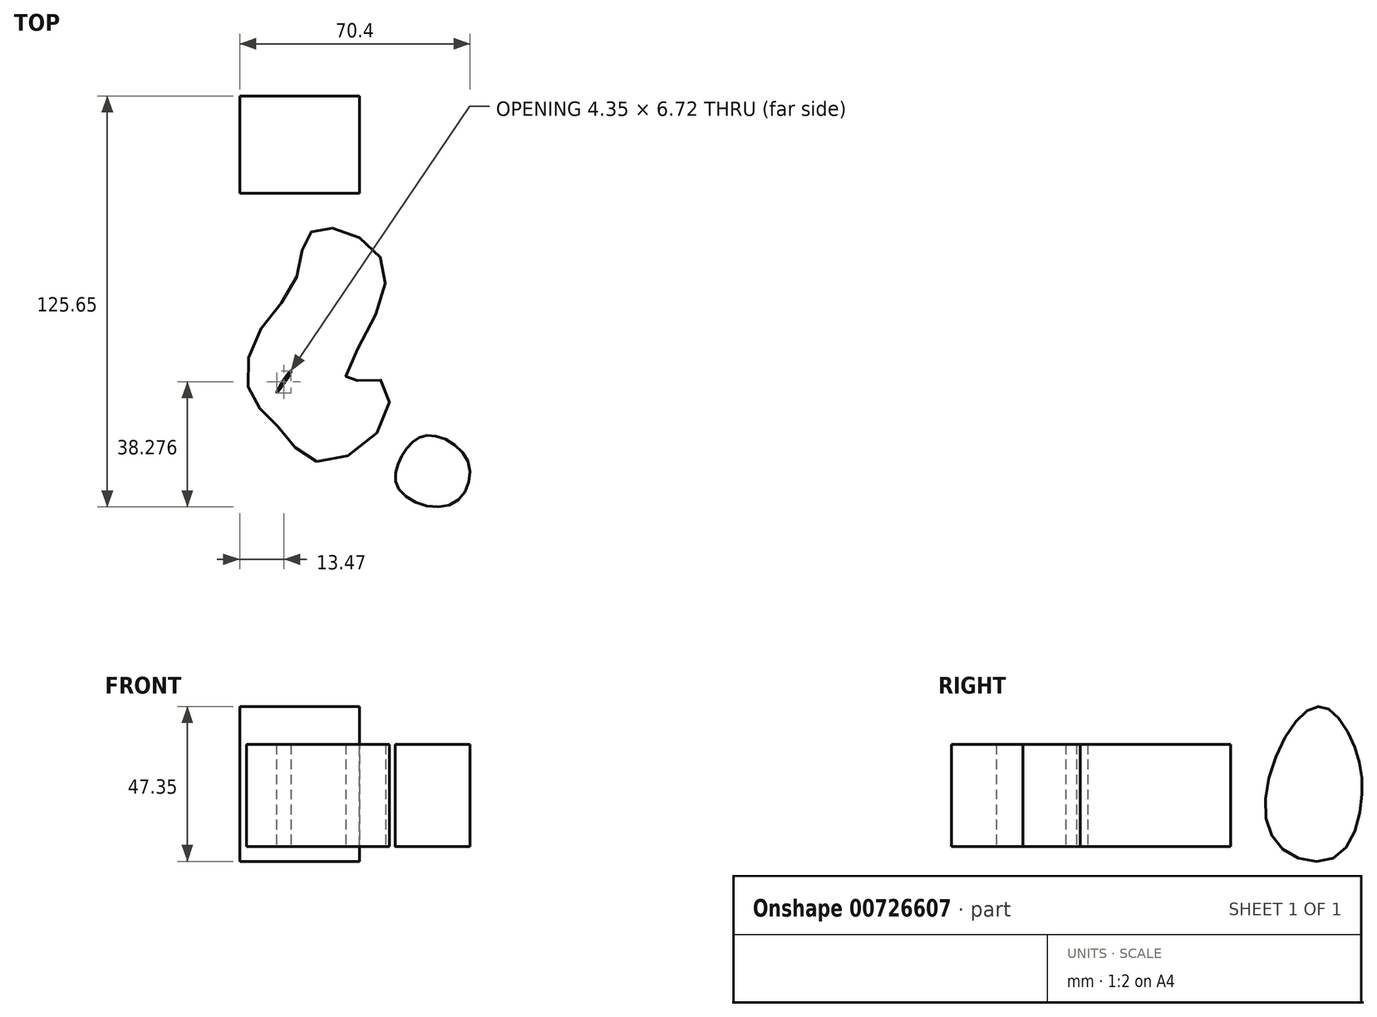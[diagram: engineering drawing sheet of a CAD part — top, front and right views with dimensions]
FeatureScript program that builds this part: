
annotation { "Feature Type Name" : "Feature", "Feature Type Description" : "" }
export const myFeature = defineFeature(function(context is Context, id is Id, definition is map)
    precondition{}
    {
        {
            var Q0;
            Q0=qCreatedBy(makeId("Top.planeOp"),FACE);
            var sketch = newSketch(context, id + "F0", { "sketchPlane" : qUnion([Q0])});
            skFitSpline(sketch, "E0", {"points": [v(23.55, -40.1) * mm, v(44.04, -28.28) * mm, v(42.47, -14.88) * mm, v(32.81, -15.47) * mm, v(39.9, 1.48) * mm, v(43.65, 21.18) * mm, v(29.86, 31.04) * mm, v(20.6, 28.87) * mm, v(17.24, 15.67) * mm, v(4.83, -2.27) * mm, v(3.45, -20) * mm, v(12.32, -30.05) * mm, v(23.55, -40.1) * mm]});
            skFitSpline(sketch, "E1", {"points": [v(48.7, -48.67) * mm, v(49.87, -37.83) * mm, v(57.76, -32.11) * mm, v(69.78, -40.1) * mm, v(64.65, -53.2) * mm, v(48.7, -48.67) * mm]});
            skFitSpline(sketch, "E2", {"points": [v(11.3, -19.1) * mm, v(15.69, -12.57) * mm, v(15.44, -12.44) * mm, v(11.3, -19.1) * mm]});
            skSolve(sketch);
        }
        {
            var Q0;
            Q0 = qSketchRegion(id + "F0", true);
            extrude(context, id + "F1", {"entities" : qUnion([Q0]), "depth" : 31.24 * mm, "offsetDistance" : 25.4 * mm});
        }
        {
            var Q0;
            Q0=qCreatedBy(makeId("Right.planeOp"),FACE);
            var sketch = newSketch(context, id + "F2", { "sketchPlane" : qUnion([Q0])});
            skFitSpline(sketch, "E3", {"points": [v(61.4, 42.03) * mm, v(69.48, 30.01) * mm, v(71.45, 14.45) * mm, v(63.56, -3.1) * mm, v(46.42, 0) * mm, v(42.87, 20.16) * mm, v(54.1, 41.05) * mm, v(61.4, 42.03) * mm]});
            skFitSpline(sketch, "E4", {"points": [v(56.27, 27.25) * mm, v(63.76, 23.9) * mm, v(62.97, 15.82) * mm, v(58.83, 8.34) * mm, v(51.54, 13.07) * mm, v(52.33, 22.33) * mm, v(56.27, 27.25) * mm]});
            skSolve(sketch);
        }
        {
            var Q0;
            Q0=makeQuery(id+"F2.imprint","IMPRINT",FACE,{"disambiguationData":[TD([[makeQuery(id+"F2.imprint","IMPRINT",EDGE,{"derivedFrom":sQuery(id+"F2.wireOp",EDGE,"E3")}),-1.0]])]});
            var Q1;
            Q1=makeQuery(id+"F2.imprint","IMPRINT",FACE,{"disambiguationData":[TD([[makeQuery(id+"F2.imprint","IMPRINT",EDGE,{"derivedFrom":sQuery(id+"F2.wireOp",EDGE,"E4")}),-1.0]])]});
            extrude(context, id + "F3", {"entities" : qUnion([Q0, Q1]), "depth" : 11.18 * mm, "offsetDistance" : 25.4 * mm});
        }
        {
            var Q0;
            Q0=makeQuery(id+"F3.opExtrude","CAP_FACE",FACE,{"disambiguationData":[OSD([sQuery(id+"F2.wireOp",EDGE,"E3")])],"isStart":true});
            var Q1;
            Q1=makeQuery(id+"F3.opExtrude","CAP_FACE",FACE,{"disambiguationData":[OSD([sQuery(id+"F2.wireOp",EDGE,"E3")])],"isStart":false});
            extrude(context, id + "F4", {"entities" : qUnion([Q0, Q1]), "operationType" : NewBodyOperationType.ADD, "oppositeDirection" : true, "depth" : 25.4 * mm, "offsetDistance" : 25.4 * mm});
        }
    });
